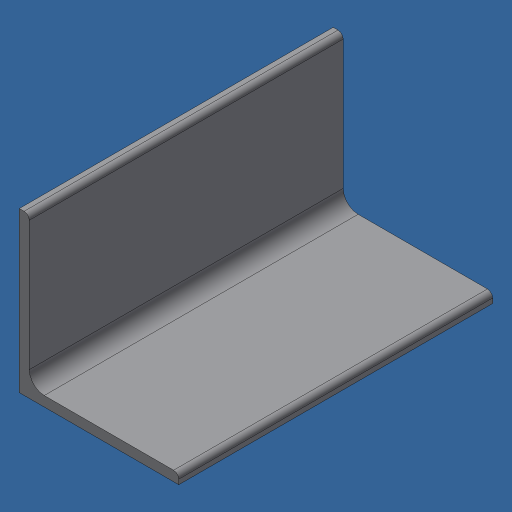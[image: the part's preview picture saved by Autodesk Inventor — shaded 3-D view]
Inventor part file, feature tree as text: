
AUTODESK INVENTOR PART (.ipt)
format: ipt  version: 2024.3 (Build 283343000, 343)  size: 109,056 bytes
history: native  units: mm (DEFAULTED — no unit token found)
features: other x1, extrude x1
ambient origin geometry x8: Origin, YZ Plane, XZ Plane, XY Plane, X Axis, Y Axis, Z Axis, Center Point
bodies: Body1 (feature_tree)
feature tree (2):
  other  "Finish - None"
  extrude  "2" X 2" X 1/8""  Depth=3.175mm
